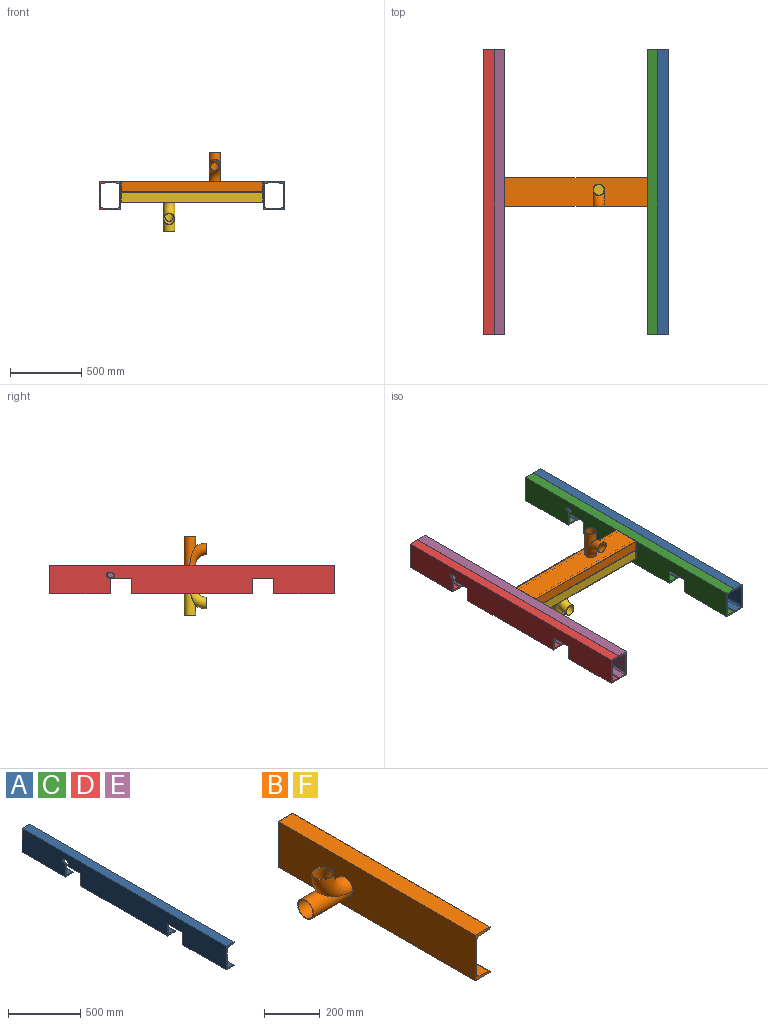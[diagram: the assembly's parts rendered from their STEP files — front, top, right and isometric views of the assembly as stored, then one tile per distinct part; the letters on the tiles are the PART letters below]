
ASSEMBLY  parts=6 mates=5
PART A: 31 faces, bbox 103.3x2000x200 mm
  f0: plane 425x75mm, normal (0,0,-1), area 31875mm2, adj f7,f8,f23,f27
  f1: plane 850x75mm, normal (0,0,-1), area 63750mm2, adj f7,f9,f24,f28
  f2: plane 425x50.39mm, normal (0.08,0,1), area 21485.9mm2, adj f4,f10,f23,f27
  f3: plane 850x50.39mm, normal (0.08,0,1), area 42971.8mm2, adj f5,f11,f24,f28
  f4: cylinder r=11.5mm len=425mm, axis (0,1,0), area 7287.4mm2, adj f2,f6,f23,f27
  f5: cylinder r=11.5mm len=850mm, axis (0,1,0), area 14574.9mm2, adj f3,f6,f24,f28
  f6: plane 2000x151.13mm, normal (1,0,0), area 276311.6mm2, adj f4,f5,f13,f14,f22,f23,f24,f25
  f7: plane 2000x200mm, normal (-1,0,0), area 366722.8mm2, adj f0,f1,f18,f19,f22,f23,f24,f25
  f8: plane 425x2.96mm, normal (1,0,0), area 1259.3mm2, adj f0,f10,f23,f27
  f9: plane 850x2.96mm, normal (1,0,0), area 2518.6mm2, adj f1,f11,f24,f28
  f10: cylinder r=6mm len=425mm, axis (0,1,0), area 3802.1mm2, adj f2,f8,f23,f27
  f11: cylinder r=6mm len=850mm, axis (0,1,0), area 7604.3mm2, adj f3,f9,f24,f28
  f12: plane 425x50.39mm, normal (0.08,0,1), area 21485.9mm2, adj f13,f21,f22,f25
  f13: cylinder r=11.5mm len=425mm, axis (0,1,0), area 7287.4mm2, adj f6,f12,f22,f25
  f14: cylinder r=11.5mm len=2000mm, axis (0,1,0), area 34293.8mm2, adj f6,f15,f22,f23
  f15: plane 2000x50.39mm, normal (0.08,0,-1), area 101110.2mm2, adj f14,f16,f22,f23
  f16: cylinder r=6mm len=2000mm, axis (0,1,0), area 17892.4mm2, adj f15,f17,f22,f23
  f17: plane 2000x2.96mm, normal (1,0,0), area 5926.1mm2, adj f16,f18,f22,f23
  f18: plane 2000x75mm, normal (0,0,1), area 150000mm2, adj f7,f17,f22,f23
  f19: plane 425x75mm, normal (0,0,-1), area 31875mm2, adj f7,f20,f22,f25
  f20: plane 425x2.96mm, normal (1,0,0), area 1259.3mm2, adj f19,f21,f22,f25
  f21: cylinder r=6mm len=425mm, axis (0,1,0), area 3802.1mm2, adj f12,f20,f22,f25
  f22: plane 200x75mm, normal (0,-1,0), area 3218.5mm2, adj f6,f7,f12,f13,f14,f15,f16,f17
  f23: plane 200x75mm, normal (0,1,0), area 3218.5mm2, adj f0,f2,f4,f6,f7,f8,f10,f14
  f24: plane 105x75mm, normal (0,-1,0), area 1651.8mm2, adj f1,f3,f5,f6,f7,f9,f11,f26
  f25: plane 105x75mm, normal (0,1,0), area 1651.8mm2, adj f6,f7,f12,f13,f19,f20,f21,f26
  f26: plane 150x8.5mm, normal (0,0,-1), area 1275mm2, adj f6,f7,f24,f25
  f27: plane 105x75mm, normal (0,-1,0), area 1651.8mm2, adj f0,f2,f4,f6,f7,f8,f10,f29
  f28: plane 105x75mm, normal (0,1,0), area 1651.8mm2, adj f1,f3,f5,f6,f7,f9,f11,f29
  f29: plane 150x8.5mm, normal (0,0,-1), area 1275mm2, adj f6,f7,f27,f28
  f30: cylinder r=20mm len=65.27mm, axis (-0.71,0.71,0), area 1510.6mm2, adj f6,f7
PART B: 35 faces, bbox 275x1000x200 mm
  f0: torus R=115mm, axis (0,-1,0), area 30321.9mm2, adj f9,f15,f16
  f1: plane 1000x50.39mm, normal (0.08,0,1), area 50555.1mm2, adj f2,f12,f13,f14
  f2: cylinder r=11.5mm len=1000mm, axis (0,1,0), area 17146.9mm2, adj f1,f3,f13,f14
  f3: plane 1000x151.13mm, normal (1,0,0), area 146711.2mm2, adj f2,f4,f13,f14,f34
  f4: cylinder r=11.5mm len=1000mm, axis (0,1,0), area 17146.9mm2, adj f3,f5,f13,f14
  f5: plane 1000x50.39mm, normal (0.08,0,-1), area 50555.1mm2, adj f4,f6,f13,f14
  f6: cylinder r=6mm len=1000mm, axis (0,1,0), area 8946.2mm2, adj f5,f7,f13,f14
  f7: plane 1000x2.96mm, normal (1,0,0), area 2963mm2, adj f6,f8,f13,f14
  f8: plane 1000x75mm, normal (0,0,1), area 75000mm2, adj f7,f9,f13,f14
  f9: plane 1000x200mm, normal (-1,0,0), area 194973.5mm2, adj f0,f8,f10,f13,f14,f16
  f10: plane 1000x75mm, normal (0,0,-1), area 75000mm2, adj f9,f11,f13,f14
  f11: plane 1000x2.96mm, normal (1,0,0), area 2963mm2, adj f10,f12,f13,f14
  f12: cylinder r=6mm len=1000mm, axis (0,1,0), area 8946.2mm2, adj f1,f11,f13,f14
  f13: plane 200x75mm, normal (0,-1,0), area 3218.5mm2, adj f1,f2,f3,f4,f5,f6,f7,f8
  f14: plane 200x75mm, normal (0,1,0), area 3218.5mm2, adj f1,f2,f3,f4,f5,f6,f7,f8
  f15: plane 80x80mm, normal (0,0,1), area 608.7mm2, adj f0,f18
  f16: cylinder r=40mm len=200mm, axis (1,0,0), area 37265mm2, adj f0,f9,f17
  f17: plane 80x80mm, normal (-1,0,0), area 608.7mm2, adj f16,f33
  f18: torus R=115mm, axis (0,-1,0), area 29274.9mm2, adj f15,f27,f33
  f19: plane 995x50.39mm, normal (-0.08,0,-1), area 50302.3mm2, adj f20,f30,f31,f32
  f20: cylinder r=14mm len=995mm, axis (0,1,0), area 20770.1mm2, adj f19,f21,f31,f32
  f21: plane 995x151.13mm, normal (-1,0,0), area 145955.5mm2, adj f20,f22,f31,f32,f34
  f22: cylinder r=14mm len=995mm, axis (0,1,0), area 20770.1mm2, adj f21,f23,f31,f32
  f23: plane 995x50.39mm, normal (-0.08,0,1), area 50302.3mm2, adj f22,f24,f31,f32
  f24: cylinder r=3.5mm len=995mm, axis (0,1,0), area 5192.5mm2, adj f23,f25,f31,f32
  f25: plane 995x0.46mm, normal (-1,0,0), area 460.7mm2, adj f24,f26,f31,f32
  f26: plane 995x70mm, normal (0,0,-1), area 69650mm2, adj f25,f27,f31,f32
  f27: plane 995x195mm, normal (1,0,0), area 189604.8mm2, adj f18,f26,f28,f31,f32,f33
  f28: plane 995x70mm, normal (0,0,1), area 69650mm2, adj f27,f29,f31,f32
  f29: plane 995x0.46mm, normal (-1,0,0), area 460.7mm2, adj f28,f30,f31,f32
  f30: cylinder r=3.5mm len=995mm, axis (0,1,0), area 5192.5mm2, adj f19,f29,f31,f32
  f31: plane 195x70mm, normal (0,1,0), area 1592.7mm2, adj f19,f20,f21,f22,f23,f24,f25,f26
  f32: plane 195x70mm, normal (0,-1,0), area 1592.7mm2, adj f19,f20,f21,f22,f23,f24,f25,f26
  f33: cylinder r=37.5mm len=202.5mm, axis (1,0,0), area 35621.9mm2, adj f17,f18,f27
  f34: cylinder r=37.5mm len=75mm, axis (-1,0,0), area 589mm2, adj f3,f21
PART C: same geometry as A
PART D: same geometry as A
PART E: same geometry as A
PART F: same geometry as B
PLACE A rot(axis=(0,0,1),180deg) t=(-552.82,-283.39,587.13)mm
PLACE B rot(axis=(0.58,0.58,-0.58),120deg) t=(-1165.32,-283.39,649.63)mm
PLACE C t=(-627.82,-283.39,587.13)mm
PLACE D t=(-1777.82,-283.39,587.13)mm
PLACE E rot(axis=(0,0,1),180deg) t=(-1702.82,-283.39,587.13)mm
PLACE F rot(axis=(0.58,-0.58,0.58),120deg) t=(-1165.32,-283.39,574.63)mm
MATE fastened B.f14 <-> C.f7  axis (1,0,0) through (-665.32,-283.39,687.13)mm
MATE fastened B.f7 <-> F.f7  axis (0,0,-1) through (-1665.32,-383.39,612.13)mm
MATE fastened D.f17 <-> E.f17  axis (1,0,0) through (-1740.32,-1283.39,687.13)mm
MATE fastened E.f7 <-> B.f13  axis (1,0,0) through (-1665.32,-283.39,687.13)mm
MATE fastened A.f17 <-> C.f17  axis (-1,0,0) through (-590.32,-1283.39,687.13)mm
